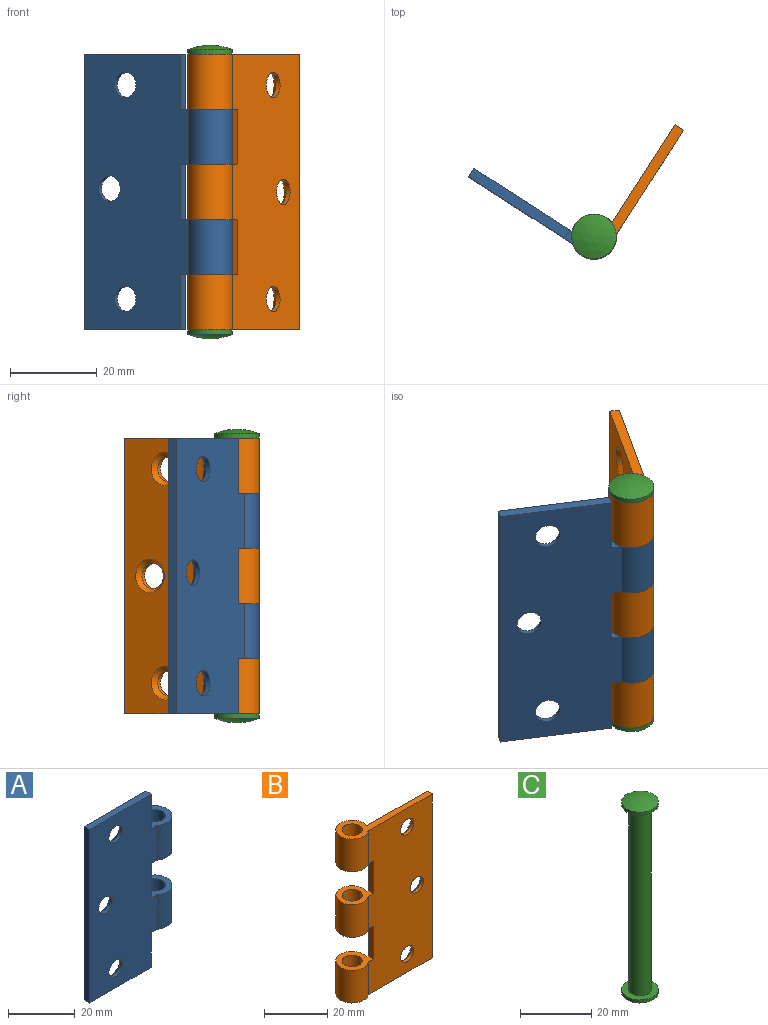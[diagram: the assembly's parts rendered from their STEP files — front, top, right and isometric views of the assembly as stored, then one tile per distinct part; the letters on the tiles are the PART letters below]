
ASSEMBLY  parts=3 mates=2
PART A: 22 faces, bbox 36.9x10.3x63.5 mm
  f0: cylinder r=3.17mm len=12.7mm, axis (0,0,-1), area 253.4mm2, adj f20,f21
  f1: cylinder r=5.16mm len=12.7mm, axis (0,0,-1), area 375.3mm2, adj f13,f15,f20,f21
  f2: cylinder r=3.17mm len=12.7mm, axis (0,0,-1), area 253.4mm2, adj f18,f19
  f3: cylinder r=5.16mm len=12.7mm, axis (0,0,-1), area 375.3mm2, adj f13,f15,f18,f19
  f4: cone r=2.92mm half-angle=41deg, axis (0,1,0), area 32.5mm2, adj f5,f15
  f5: cylinder r=2.92mm len=5.84mm, axis (0,1,0), area 21mm2, adj f4,f13
  f6: cone r=2.92mm half-angle=41deg, axis (0,1,0), area 32.5mm2, adj f9,f15
  f7: cone r=2.92mm half-angle=41deg, axis (0,1,0), area 32.5mm2, adj f8,f15
  f8: cylinder r=2.92mm len=5.84mm, axis (0,1,0), area 21mm2, adj f7,f13
  f9: cylinder r=2.92mm len=5.84mm, axis (0,1,0), area 21mm2, adj f6,f13
  f10: plane 12.7x2.29mm, normal (1,0,0), area 29mm2, adj f13,f15,f18,f21
  f11: plane 12.7x2.29mm, normal (1,0,0), area 29mm2, adj f13,f15,f16,f20
  f12: plane 63.5x2.29mm, normal (-1,0,0), area 145.2mm2, adj f13,f15,f16,f17
  f13: plane 63.5x28.58mm, normal (0,-1,0), area 1644mm2, adj f1,f3,f5,f8,f9,f10,f11,f12
  f14: plane 12.7x2.29mm, normal (1,0,0), area 29mm2, adj f13,f15,f17,f19
  f15: plane 63.5x26.91mm, normal (0,1,0), area 1537.6mm2, adj f1,f3,f4,f6,f7,f10,f11,f12
  f16: plane 26.21x2.29mm, normal (0,0,1), area 59.9mm2, adj f11,f12,f13,f15
  f17: plane 26.21x2.29mm, normal (0,0,-1), area 59.9mm2, adj f12,f13,f14,f15
  f18: plane 10.7x10.32mm, normal (0,0,1), area 55.1mm2, adj f2,f3,f10,f13,f15
  f19: plane 10.7x10.32mm, normal (0,0,-1), area 55.1mm2, adj f2,f3,f13,f14,f15
  f20: plane 10.7x10.32mm, normal (0,0,1), area 55.1mm2, adj f0,f1,f11,f13,f15
  f21: plane 10.7x10.32mm, normal (0,0,-1), area 55.1mm2, adj f0,f1,f10,f13,f15
PART B: 23 faces, bbox 36.9x10.3x63.5 mm
  f0: cone r=2.92mm half-angle=41deg, axis (0,1,0), area 32.5mm2, adj f1,f12
  f1: cylinder r=2.92mm len=5.84mm, axis (0,1,0), area 21mm2, adj f0,f16
  f2: cone r=2.92mm half-angle=41deg, axis (0,1,0), area 32.5mm2, adj f3,f12
  f3: cylinder r=2.92mm len=5.84mm, axis (0,1,0), area 21mm2, adj f2,f16
  f4: cone r=2.92mm half-angle=41deg, axis (0,1,0), area 32.5mm2, adj f5,f12
  f5: cylinder r=2.92mm len=5.84mm, axis (0,1,0), area 21mm2, adj f4,f16
  f6: cylinder r=3.17mm len=12.7mm, axis (0,0,-1), area 253.4mm2, adj f13,f22
  f7: cylinder r=5.16mm len=12.7mm, axis (0,0,-1), area 375.3mm2, adj f12,f13,f16,f22
  f8: cylinder r=3.17mm len=12.7mm, axis (0,0,-1), area 253.4mm2, adj f14,f18
  f9: cylinder r=5.16mm len=12.7mm, axis (0,0,-1), area 375.3mm2, adj f12,f14,f16,f18
  f10: cylinder r=3.17mm len=12.7mm, axis (0,0,-1), area 253.4mm2, adj f19,f21
  f11: cylinder r=5.16mm len=12.7mm, axis (0,0,-1), area 375.3mm2, adj f12,f16,f19,f21
  f12: plane 63.5x26.91mm, normal (0,1,0), area 1546.5mm2, adj f0,f2,f4,f7,f9,f11,f13,f14
  f13: plane 36.91x10.32mm, normal (0,0,1), area 115mm2, adj f6,f7,f12,f15,f16
  f14: plane 36.91x10.32mm, normal (0,0,-1), area 115mm2, adj f8,f9,f12,f15,f16
  f15: plane 63.5x2.29mm, normal (1,0,0), area 145.2mm2, adj f12,f13,f14,f16
  f16: plane 63.5x28.58mm, normal (0,-1,0), area 1674mm2, adj f1,f3,f5,f7,f9,f11,f13,f14
  f17: plane 12.7x2.29mm, normal (-1,0,0), area 29mm2, adj f12,f16,f18,f19
  f18: plane 10.7x10.32mm, normal (0,0,1), area 55.1mm2, adj f8,f9,f12,f16,f17
  f19: plane 10.7x10.32mm, normal (0,0,-1), area 55.1mm2, adj f10,f11,f12,f16,f17
  f20: plane 12.7x2.29mm, normal (-1,0,0), area 29mm2, adj f12,f16,f21,f22
  f21: plane 10.7x10.32mm, normal (0,0,1), area 55.1mm2, adj f10,f11,f12,f16,f20
  f22: plane 10.7x10.32mm, normal (0,0,-1), area 55.1mm2, adj f6,f7,f12,f16,f20
PART C: 7 faces, bbox 10.4x10.4x67.6 mm
  f0: cylinder r=5.16mm len=10.32mm, axis (0,0,-1), area 33.3mm2, adj f4,f6
  f1: cylinder r=3.17mm len=63.5mm, axis (0,0,-1), area 1266.8mm2, adj f5,f6
  f2: cylinder r=5.16mm len=10.32mm, axis (0,0,-1), area 33.3mm2, adj f3,f5
  f3: sphere r=13.45mm, area 87mm2, adj f2
  f4: sphere r=13.45mm, area 86.9mm2, adj f0
  f5: plane 10.32x10.32mm, normal (0,0,-1), area 52mm2, adj f1,f2
  f6: plane 10.32x10.32mm, normal (0,0,1), area 52mm2, adj f0,f1
PLACE A rot(axis=(0,0,-1),32.8deg) t=(1.29,-10.61,39.38)mm
PLACE B rot(axis=(0,0,1),57.2deg) t=(1.29,-10.61,39.38)mm
PLACE C rot(axis=(0,0,1),57.2deg) t=(1.29,-10.61,39.38)mm
MATE revolute A.f0 <-> B.f6  axis (0,0,-1) through (1.29,-10.61,58.43)mm
MATE fastened B.f6 <-> C.f0  axis (0,0,1) through (1.29,-10.61,71.13)mm
